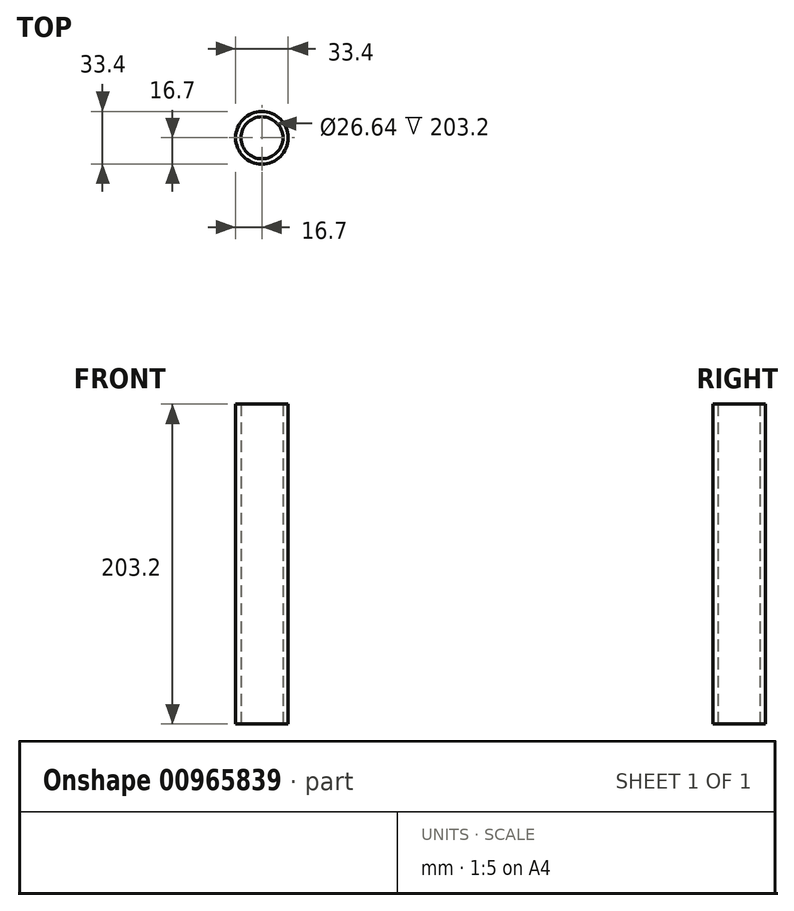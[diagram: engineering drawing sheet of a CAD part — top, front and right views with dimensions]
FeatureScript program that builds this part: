
annotation { "Feature Type Name" : "Feature", "Feature Type Description" : "" }
export const myFeature = defineFeature(function(context is Context, id is Id, definition is map)
    precondition{}
    {
        {
            var Q0;
            Q0=qCreatedBy(makeId("Top.planeOp"),FACE);
            var sketch = newSketch(context, id + "F0", { "sketchPlane" : qUnion([Q0])});
            skCircle(sketch, "E0", {"center": v(0, 0) * mm, "radius": 13.32 * mm});
            skCircle(sketch, "E1", {"center": v(0, 0) * mm, "radius": 16.7 * mm});
            skSolve(sketch);
        }
        {
            var Q0;
            Q0=makeQuery(id+"F0.imprint","IMPRINT",FACE,{"disambiguationData":[TD([[makeQuery(id+"F0.imprint","IMPRINT",EDGE,{"derivedFrom":sQuery(id+"F0.wireOp",EDGE,"E0")}),-1.0]])]});
            extrude(context, id + "F1", {"entities" : qUnion([Q0]), "depth" : 203.2 * mm, "offsetDistance" : 25.4 * mm});
        }
    });
